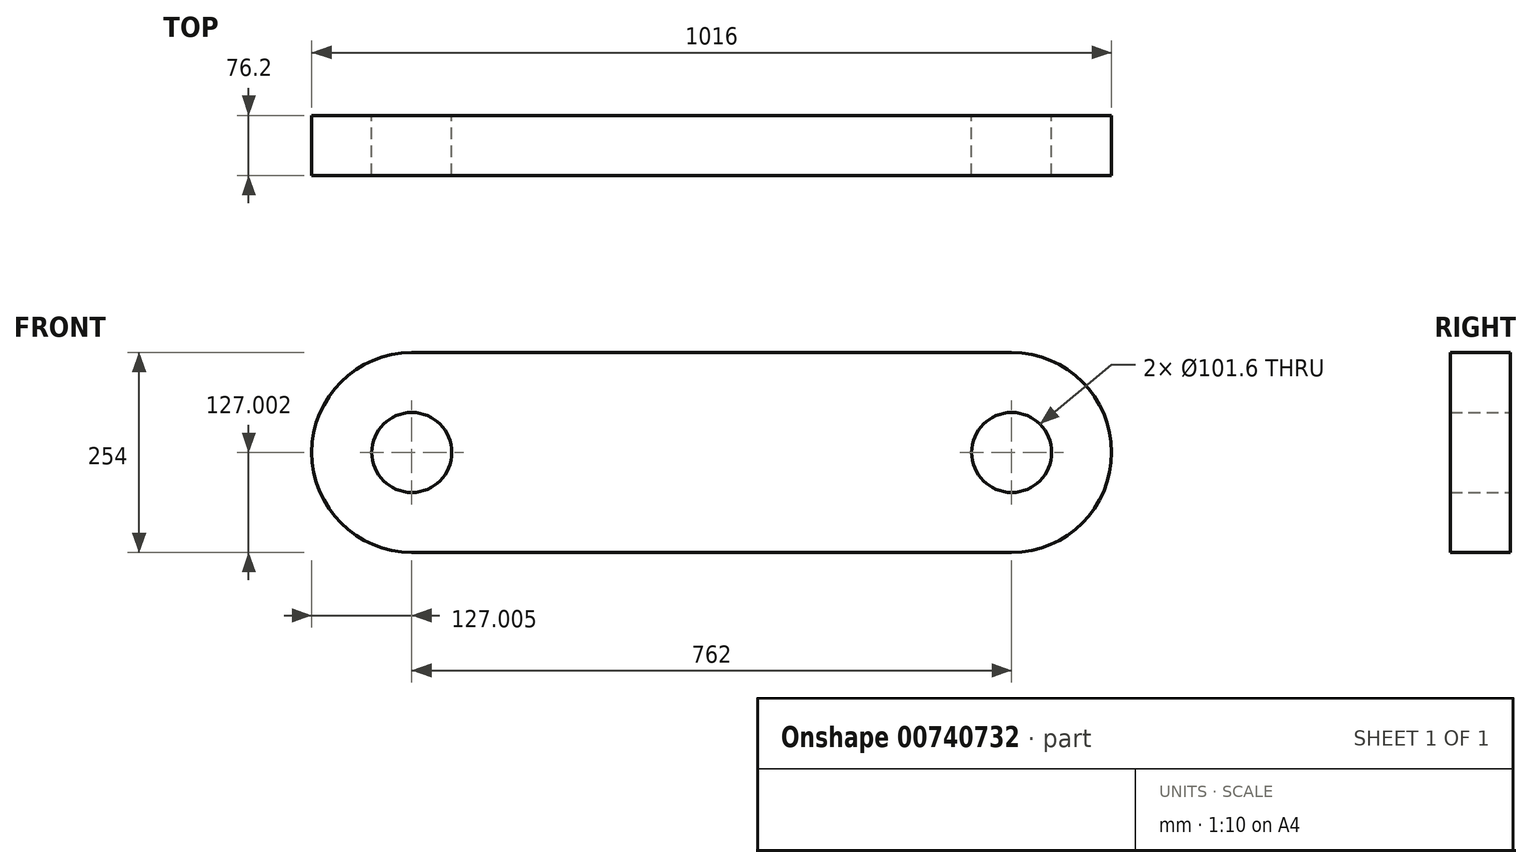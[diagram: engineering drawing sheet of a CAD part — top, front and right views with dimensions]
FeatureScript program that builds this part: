
annotation { "Feature Type Name" : "Feature", "Feature Type Description" : "" }
export const myFeature = defineFeature(function(context is Context, id is Id, definition is map)
    precondition{}
    {
        {
            var Q0;
            Q0=qCreatedBy(makeId("Front.planeOp"),FACE);
            var sketch = newSketch(context, id + "F0", { "sketchPlane" : qUnion([Q0])});
            skLineSegment(sketch, "E0", {"start": v(-385.46, 129.71) * mm, "end": v(376.54, 129.71) * mm});
            skLineSegment(sketch, "E1", {"start": v(-385.46, -124.29) * mm, "end": v(376.54, -124.29) * mm});
            skArc(sketch, "E2", {"start": v(376.54, -124.29) * mm, "mid": v(503.54, 2.71) * mm, "end": v(376.54, 129.71) * mm});
            skArc(sketch, "E3", {"start": v(-385.46, 129.71) * mm, "mid": v(-512.46, 2.71) * mm, "end": v(-385.46, -124.29) * mm});
            skCircle(sketch, "E4", {"center": v(376.54, 2.71) * mm, "radius": 50.8 * mm});
            skCircle(sketch, "E5", {"center": v(-385.46, 2.71) * mm, "radius": 50.8 * mm});
            skSolve(sketch);
        }
        {
            var Q0;
            Q0 = qSketchRegion(id + "F0", true);
            extrude(context, id + "F1", {"entities" : qUnion([Q0]), "depth" : 76.2 * mm, "offsetDistance" : 25.4 * mm});
        }
    });
